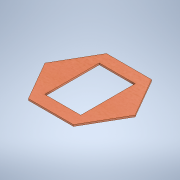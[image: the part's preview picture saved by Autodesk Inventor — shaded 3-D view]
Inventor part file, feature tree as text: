
AUTODESK INVENTOR PART (.ipt)
format: ipt  version: 2020 (Build 240168000, 168)  size: 220,672 bytes
history: native  units: mm
features: sketch x1, extrude x1
ambient origin geometry x8: Origin, YZ Plane, XZ Plane, XY Plane, X Axis, Y Axis, Z Axis, Center Point
bodies: Body1 (feature_tree)
feature tree (2):
  sketch  "Sketch6"  dims[d44=97.0mm d72=6.5mm d77=140.0mm d85=2.5mm d86=0.0mm d87=15.0mm d88=6.5mm d89=30.0mm d91=2.5mm d92=2.5mm d95=1.25mm d96=25.0mm d97=2.5mm d98=25.0mm d99=135.0deg d100=0.0mm d114=1.7mm d117=3.0mm d121=3.0mm d123=6.0mm]
  extrude  "Fronte"  Depth=2.5mm
